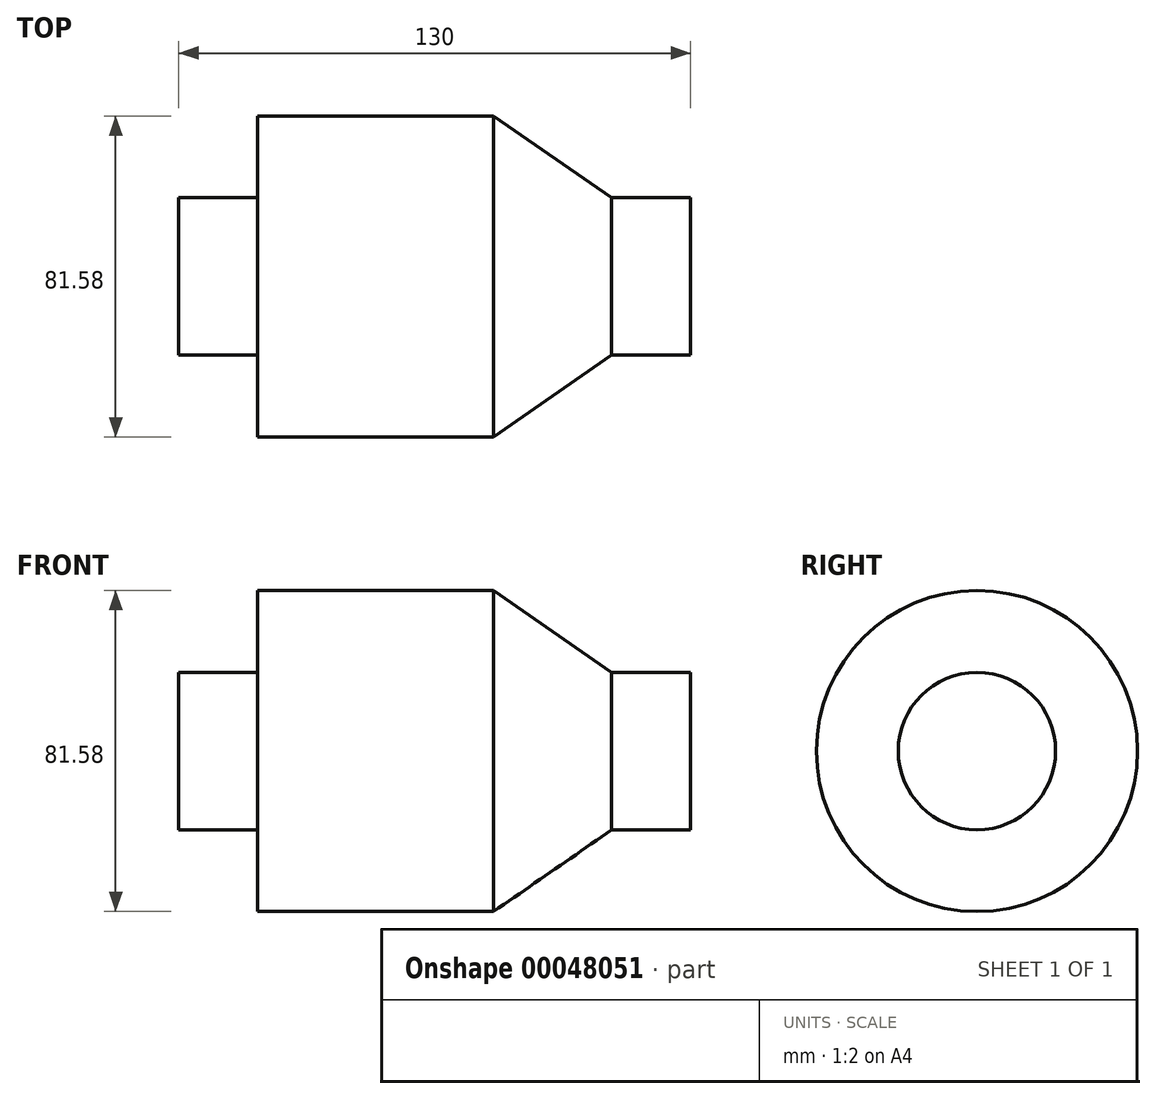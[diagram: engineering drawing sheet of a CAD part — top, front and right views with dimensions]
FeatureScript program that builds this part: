
annotation { "Feature Type Name" : "Feature", "Feature Type Description" : "" }
export const myFeature = defineFeature(function(context is Context, id is Id, definition is map)
    precondition{}
    {
        {
            var Q0;
            Q0=qCreatedBy(makeId("Front.planeOp"),FACE);
            var sketch = newSketch(context, id + "F0", { "sketchPlane" : qUnion([Q0])});
            skLineSegment(sketch, "E0", {"start": v(0, 0) * mm, "end": v(0, 20) * mm});
            skLineSegment(sketch, "E1", {"start": v(0, 20) * mm, "end": v(20, 20) * mm});
            skLineSegment(sketch, "E2", {"start": v(20, 20) * mm, "end": v(20, 40.79) * mm});
            skLineSegment(sketch, "E3", {"start": v(20, 40.79) * mm, "end": v(80, 40.79) * mm});
            skLineSegment(sketch, "E4", {"start": v(80, 40.79) * mm, "end": v(110, 20) * mm});
            skLineSegment(sketch, "E5", {"start": v(110, 20) * mm, "end": v(130, 20) * mm});
            skLineSegment(sketch, "E6", {"start": v(130, 20) * mm, "end": v(130, 0) * mm});
            skLineSegment(sketch, "E7", {"start": v(130, 0) * mm, "end": v(0, 0) * mm});
            skSolve(sketch);
        }
        {
            var Q0;
            Q0=makeQuery(id+"F0.imprint","IMPRINT",FACE,{"disambiguationData":[TD([[makeQuery(id+"F0.imprint","IMPRINT",EDGE,{"derivedFrom":sQuery(id+"F0.wireOp",EDGE,"E0")}),-1.0]])]});
            var Q1;
            Q1=sQuery(id+"F0.wireOp",EDGE,"E7");
            revolve(context, id + "F1", {"entities" : qUnion([Q0]), "axis" : qUnion([Q1]), "revolveType" : RevolveType.FULL});
        }
    });
